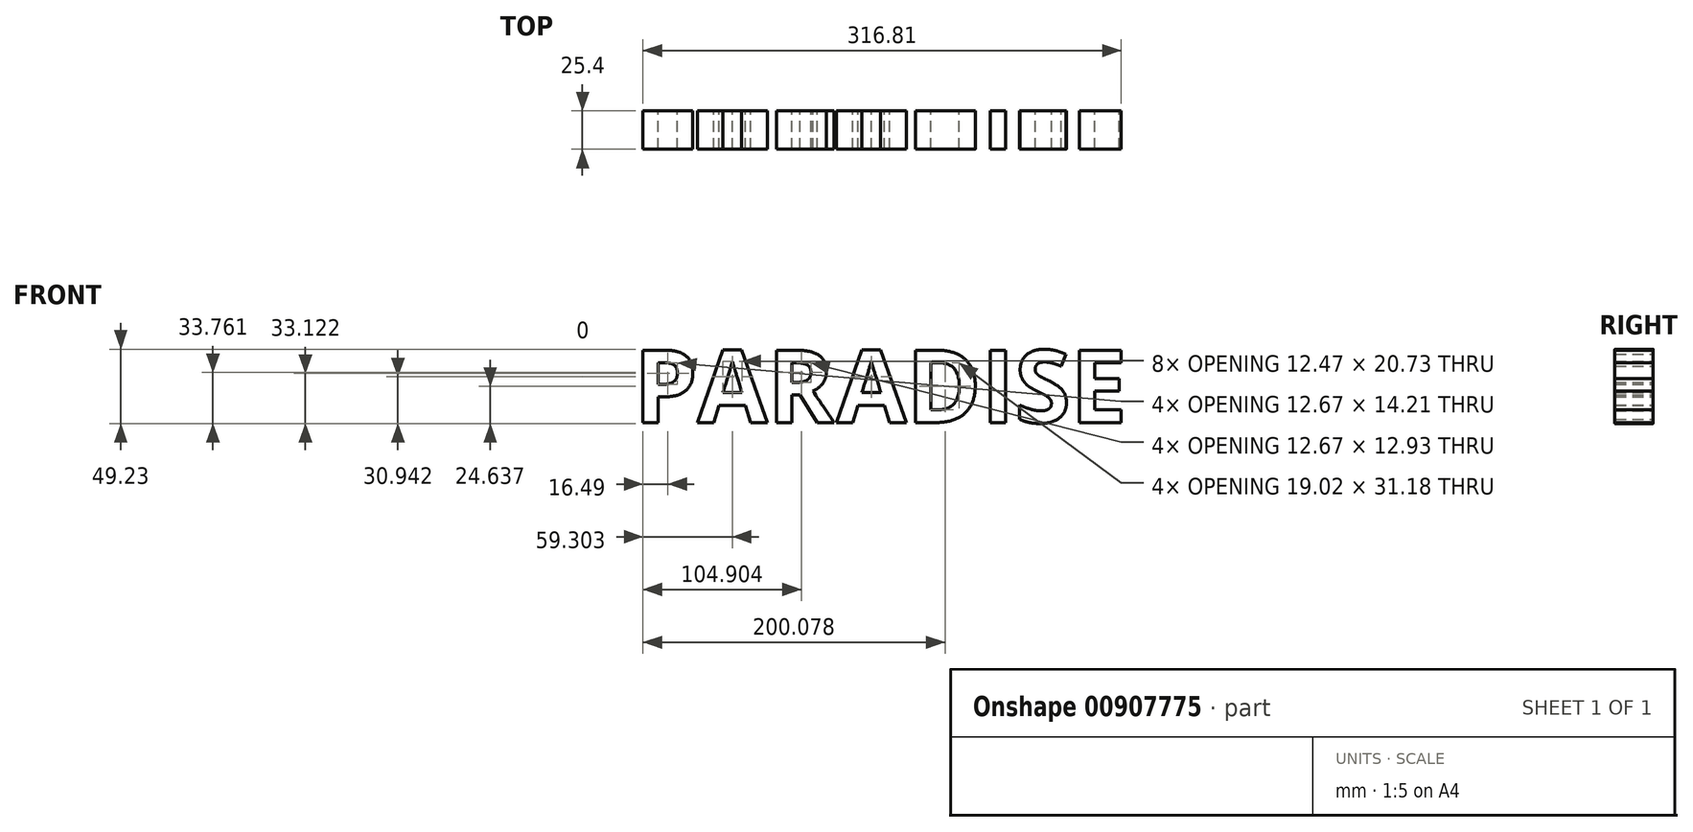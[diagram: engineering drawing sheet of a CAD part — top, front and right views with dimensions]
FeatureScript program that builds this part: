
annotation { "Feature Type Name" : "Feature", "Feature Type Description" : "" }
export const myFeature = defineFeature(function(context is Context, id is Id, definition is map)
    precondition{}
    {
        {
            var Q0;
            Q0=qCreatedBy(makeId("Front.planeOp"),FACE);
            var sketch = newSketch(context, id + "F0", { "sketchPlane" : qUnion([Q0])});
            skText(sketch, "E0", { "text": "PARADISE", "fontName": "OpenSans-Bold.ttf"});
            const initialGuessF0  = {"E0": [0, 0, 1, 0, 0.0483]};
            skSetInitialGuess(sketch, initialGuessF0);
            skSolve(sketch);
        }
        {
            var Q0;
            Q0 = qSketchRegion(id + "F0", true);
            extrude(context, id + "F1", {"entities" : qUnion([Q0]), "depth" : 25.4 * mm, "offsetDistance" : 25.4 * mm});
        }
    });
